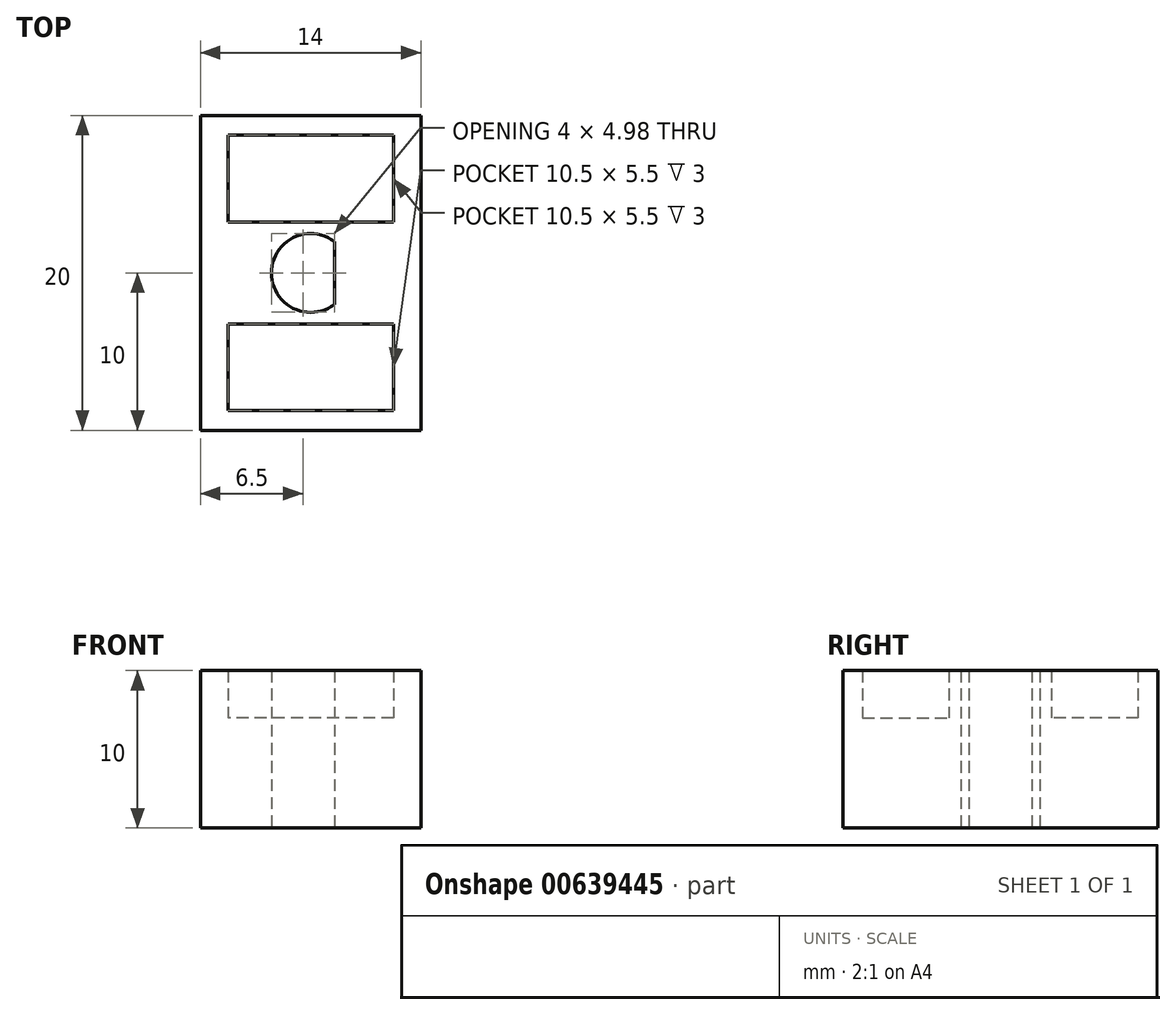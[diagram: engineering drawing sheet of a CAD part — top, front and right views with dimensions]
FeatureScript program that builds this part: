
annotation { "Feature Type Name" : "Feature", "Feature Type Description" : "" }
export const myFeature = defineFeature(function(context is Context, id is Id, definition is map)
    precondition{}
    {
        {
            var Q0;
            Q0=qCreatedBy(makeId("Top.planeOp"),FACE);
            var sketch = newSketch(context, id + "F0", { "sketchPlane" : qUnion([Q0])});
            skLineSegment(sketch, "E0.bottom", {"start": v(7, -10) * mm, "end": v(-7, -10) * mm});
            skLineSegment(sketch, "E0.top", {"start": v(7, 10) * mm, "end": v(-7, 10) * mm});
            skLineSegment(sketch, "E0.left", {"start": v(7, -10) * mm, "end": v(7, 10) * mm});
            skLineSegment(sketch, "E0.right", {"start": v(-7, -10) * mm, "end": v(-7, 10) * mm});
            skPoint(sketch, "E0.middle", {"position": v(0, 0) * mm});
            skLineSegment(sketch, "E1.bottom", {"start": v(5.25, -8.75) * mm, "end": v(-5.25, -8.75) * mm});
            skLineSegment(sketch, "E1.top", {"start": v(5.25, -3.25) * mm, "end": v(-5.25, -3.25) * mm});
            skLineSegment(sketch, "E1.left", {"start": v(5.25, -8.75) * mm, "end": v(5.25, -3.25) * mm});
            skLineSegment(sketch, "E1.right", {"start": v(-5.25, -8.75) * mm, "end": v(-5.25, -3.25) * mm});
            skPoint(sketch, "E1.middle", {"position": v(0, -6) * mm});
            skLineSegment(sketch, "E2.MirrorCS", {"start": v(5.25, 3.25) * mm, "end": v(-5.25, 3.25) * mm});
            skLineSegment(sketch, "E3.MirrorCS", {"start": v(5.25, 8.75) * mm, "end": v(5.25, 3.25) * mm});
            skLineSegment(sketch, "E4.MirrorCS", {"start": v(5.25, 8.75) * mm, "end": v(-5.25, 8.75) * mm});
            skLineSegment(sketch, "E5.MirrorCS", {"start": v(-5.25, 8.75) * mm, "end": v(-5.25, 3.25) * mm});
            skArc(sketch, "E6", {"start": v(1.5, 2) * mm, "mid": v(-2.5, 0) * mm, "end": v(1.5, -2) * mm});
            skLineSegment(sketch, "E7", {"start": v(1.5, 2) * mm, "end": v(1.5, -2) * mm});
            skSolve(sketch);
        }
        {
            var Q0;
            Q0=makeQuery(id+"F0.imprint","IMPRINT",FACE,{"disambiguationData":[TD([[makeQuery(id+"F0.imprint","IMPRINT",EDGE,{"derivedFrom":sQuery(id+"F0.wireOp",EDGE,"E0.bottom")}),-1.0]])]});
            extrude(context, id + "F1", {"entities" : qUnion([Q0]), "depth" : 10 * mm, "offsetDistance" : 25 * mm});
        }
        {
            var Q0;
            Q0=makeQuery(id+"F0.imprint","IMPRINT",FACE,{"disambiguationData":[TD([[makeQuery(id+"F0.imprint","IMPRINT",EDGE,{"derivedFrom":sQuery(id+"F0.wireOp",EDGE,"E2.MirrorCS")}),-1.0]])]});
            var Q1;
            Q1=makeQuery(id+"F0.imprint","IMPRINT",FACE,{"disambiguationData":[TD([[makeQuery(id+"F0.imprint","IMPRINT",EDGE,{"derivedFrom":sQuery(id+"F0.wireOp",EDGE,"E1.bottom")}),-1.0]])]});
            extrude(context, id + "F2", {"entities" : qUnion([Q0, Q1]), "operationType" : NewBodyOperationType.ADD, "depth" : 7 * mm, "offsetDistance" : 25 * mm});
        }
    });
